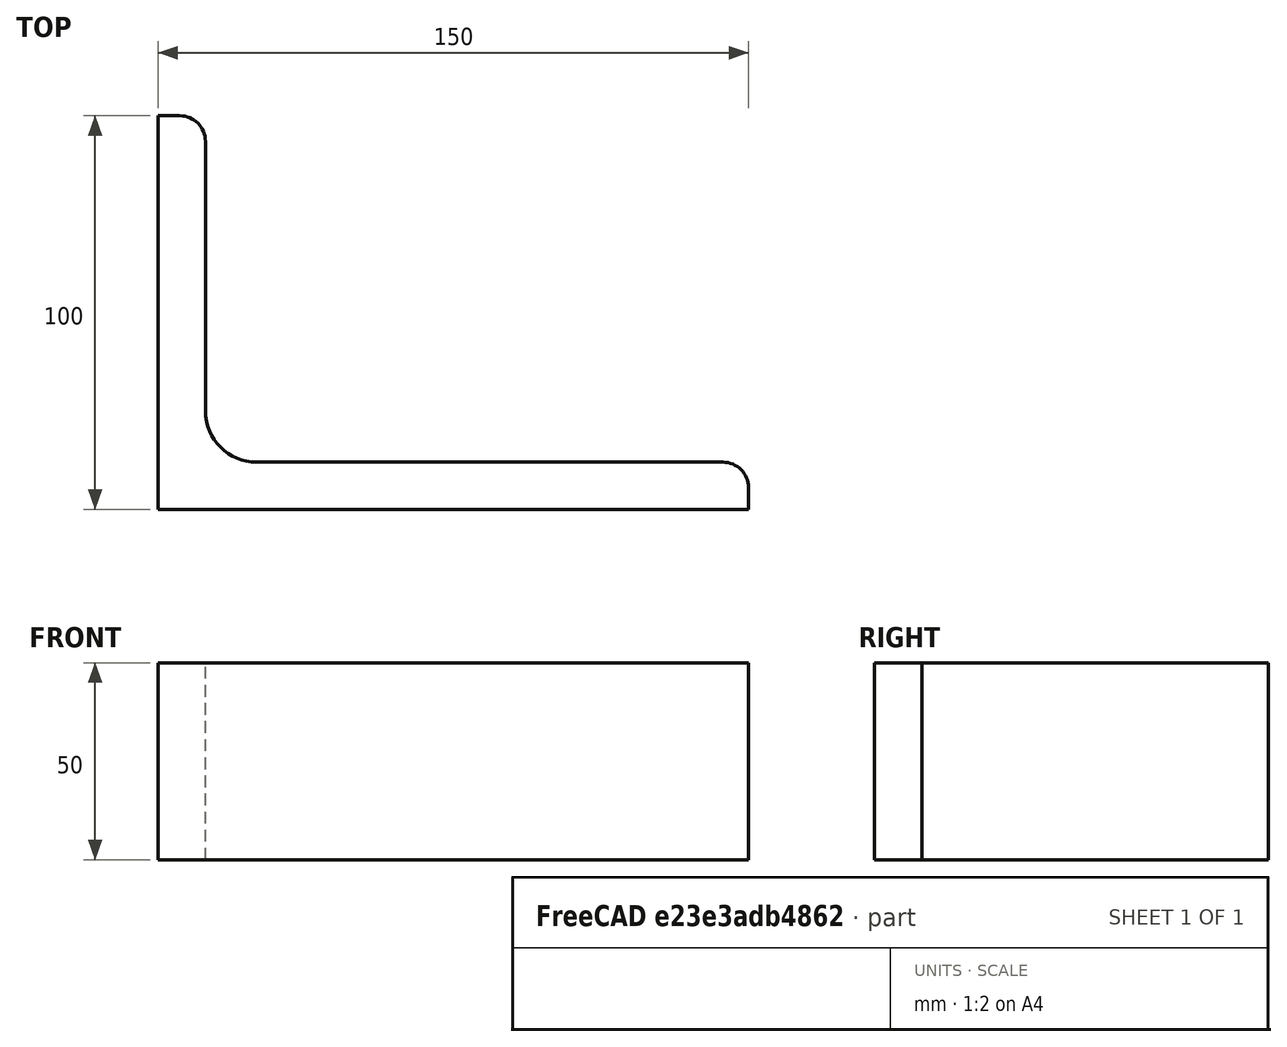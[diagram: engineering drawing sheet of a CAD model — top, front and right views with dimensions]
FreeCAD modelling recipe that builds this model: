
FCSTD DOCUMENT  (FreeCAD 0.15R4671 (Git))
Label: Angle Bar 150x100x12 EN10056 S235JR
License: All rights reserved
LicenseURL: http://en.wikipedia.org/wiki/All_rights_reserved
objects: Sketcher::SketchObject×1, Part::Extrusion×1
note: 2 computed .brp shape members not serialized (recipe doc carries the construction recipe); baked Part::Feature solids carry a one-line shape summary decoded from their .brp

FEATURE [Sketcher::SketchObject] Sketch
  sketch-geometry (9):
    g0: LineSegment StartX=0 StartY=0 StartZ=0 EndX=150 EndY=0 EndZ=0
    g1: LineSegment StartX=150 StartY=0 StartZ=0 EndX=150 EndY=5.5 EndZ=0
    g2: LineSegment StartX=143.5 StartY=12 StartZ=0 EndX=25 EndY=12 EndZ=0
    g3: LineSegment StartX=0 StartY=0 StartZ=0 EndX=0 EndY=100 EndZ=0
    g4: LineSegment StartX=0 StartY=100 StartZ=0 EndX=5.5 EndY=100 EndZ=0
    g5: LineSegment StartX=12 StartY=93.5 StartZ=0 EndX=12 EndY=25 EndZ=0
    g6: ArcOfCircle CenterX=25 CenterY=25 CenterZ=0 NormalX=0 NormalY=0 NormalZ=1 Radius=13 StartAngle=3.14159 EndAngle=4.71239
    g7: ArcOfCircle CenterX=5.5 CenterY=93.5 CenterZ=0 NormalX=0 NormalY=0 NormalZ=1 Radius=6.5 StartAngle=0 EndAngle=1.5708
    g8: ArcOfCircle CenterX=143.5 CenterY=5.5 CenterZ=0 NormalX=0 NormalY=0 NormalZ=1 Radius=6.5 StartAngle=0 EndAngle=1.5708
  constraints (23):
    c: Coincident(g0,g-1)
    c: Horizontal(g0)
    c: Coincident(g1,g0)
    c: Vertical(g1)
    c: Horizontal(g2)
    c: Coincident(g3,g-1)
    c: Vertical(g3)
    c: Coincident(g4,g3)
    c: Horizontal(g4)
    c: Vertical(g5)
    c: Tangent(g5,g6) = -1.5708
    c: Tangent(g2,g6) = 1.5708
    c: Tangent(g4,g7) = 1.5708
    c: Tangent(g5,g7) = 1.5708
    c: Tangent(g2,g8) = -1.5708
    c: Tangent(g1,g8) = -1.5708
    c: DistanceX(g0) = 150
    c: DistanceY(g3) = 100
    c: DistanceY(g0,g2) = 12
    c: DistanceX(g3,g5) = 12
    c: Radius(g6) = 13
    c: Radius(g8) = 6.5
    c: Radius(g7) = 6.5
FEATURE [Part::Extrusion] Extrude  label="Angle Bar 150x100x12 EN10056 S235JR"
  Base = -> Sketch
  Dir = (0,0,50)
  Solid = true
